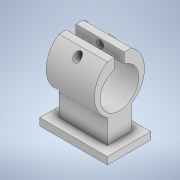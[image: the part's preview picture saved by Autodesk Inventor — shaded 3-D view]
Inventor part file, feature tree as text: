
AUTODESK INVENTOR PART (.ipt)
format: ipt  version: 2021 (Build 250183000, 183)  size: 190,976 bytes
history: native  units: in
note: dims shown in document units (in); Inventor stores cm internally (conversion verified against a paired STEP export)
features: sketch x7, extrude x4, hole x2
ambient origin geometry x8: Origin, YZ Plane, XZ Plane, XY Plane, X Axis, Y Axis, Z Axis, Center Point
bodies: Solid1 (feature_tree)
feature tree (13):
  extrude  "Extrusion1"  Depth=0.3937in
  extrude  "Extrusion4"  Depth=0.1969in
  extrude  "Extrusion5"  Depth=0.3937in
  hole  "Hole1"  [1 undecoded]
  extrude  "Extrusion6"  Depth=0.3937in
  sketch  "Sketch11"  dims[d31=0.1575in d33=0.1969in]
  hole  "Hole2"  [1 undecoded]
  sketch  "Sketch1"  dims[d0=0.1969in d1=0.3937in]
  sketch  "Sketch7"  dims[d2=0.1969in d3=0.1969in]
  sketch  "Sketch8"  dims[d4=0.3937in d5=0.2362in]
  sketch  "Sketch9"  dims[d6=0.2362in d10=0.3937in d11=0.0in]
  sketch  "Sketch10"  dims[d29=0.0984in d30=0.3937in]
  sketch  "Sketch12"  dims[d34=0.3937in d35=0.0in d36=0.0591in d37=0.0591in d39=0.0591in d40=0.3937in d41=0.0in d42=0.0315in d43=0.0419in d44=0.0837in d45=0.3937in d46=0.1969in d47=0.0591in d48=0.2362in d49=0.119in d50=0.0787in d51=0.5635in d52=0.315in d53=0.8108in d54=0.5512in d56=0.0787in d57=0.0787in d58=0.1969in d59=0.0984in d60=0.0787in d61=0.0591in d62=0.0in d63=0.2756in d64=0.1772in d65=0.3543in d66=0.1969in d67=0.1969in d68=0.2362in d69=0.119in d70=0.0787in d71=0.5635in d72=0.0591in d73=0.0in d74=0.3543in]
note: 2 required parameter values undecoded (feature->parameter linkage not recoverable at this tier; creation-order binding heuristic only, values carry confidence <= 0.55)
